# Revit family: Kabelrinne SKS - SKS 610 FT
name_source: partatom
category: Generic Models
revit_build: Autodesk Revit 2015 (Build: 20140606_1530(x64)
units: mm (PartAtom-declared; Revit-internal decimal feet)

## types (1)
- SKS 610 FT
    Article Type = SKS 610 FT
    Cut's number = 60
    Cut's number 2 = 2
    Cut's number 3 = 59
    Cut's space = 50 mm  [stored 0.164042 ft]
    GTIN = 4012196389957
    Height = 61 mm  [stored 0.200131 ft]
    Length = 3000 mm  [stored 9.84252 ft]
    Manufacturer = OBO Bettermann
    Manufacturer Art.No. = 6056636
    Material = Hot-dip galvanised
    URL = http://www.obo-bettermann.com
    Width = 100 mm  [stored 0.328084 ft]
    Width 1 = 2 mm  [stored 0.00656168 ft]
    Width 2 = 22 mm  [stored 0.0721785 ft]
    Width/2 = 50 mm  [stored 0.164042 ft]

note: [stored X ft] marks values corroborated as IEEE doubles in the binary element streams (Revit-internal decimal feet)

## geometry (parser evidence)
native form markers: Sweep x2
no freeform markers — native parametric forms only
